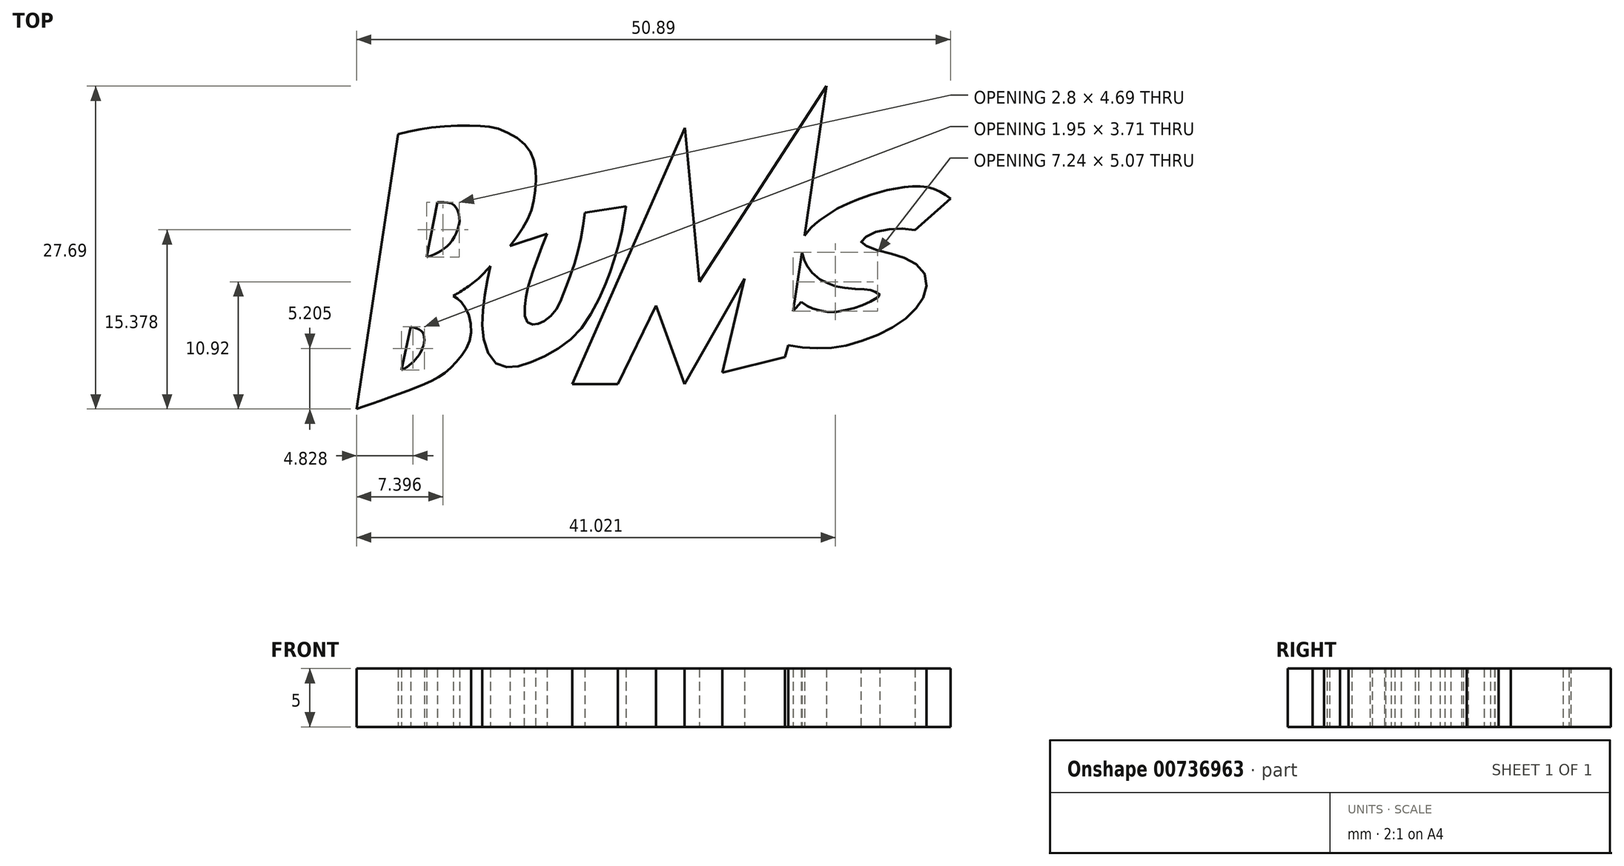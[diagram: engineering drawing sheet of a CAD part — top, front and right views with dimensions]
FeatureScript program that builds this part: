
annotation { "Feature Type Name" : "Feature", "Feature Type Description" : "" }
export const myFeature = defineFeature(function(context is Context, id is Id, definition is map)
    precondition{}
    {
        {
            var Q0;
            Q0=qCreatedBy(makeId("Top.planeOp"),FACE);
            var sketch = newSketch(context, id + "F0", { "sketchPlane" : qUnion([Q0])});
            skLineSegment(sketch, "E0", {"start": v(-15.5, -22.34) * mm, "end": v(-11.93, 1.24) * mm});
            skLineSegment(sketch, "E1", {"start": v(-11.64, -18.99) * mm, "end": v(-10.84, -15.28) * mm});
            skFitSpline(sketch, "E2", {"points": [v(-10.84, -15.28) * mm, v(-10.4, -15.42) * mm, v(-9.9, -15.69) * mm, v(-9.69, -16.35) * mm, v(-9.83, -17.08) * mm, v(-10.2, -17.8) * mm, v(-10.83, -18.47) * mm, v(-11.64, -18.99) * mm], "startDerivative": vector(3.7, -0.9) * mm, "endDerivative": vector(-6.02, -2.49) * mm});
            skLineSegment(sketch, "E3", {"start": v(-9.5, -9.3) * mm, "end": v(-8.56, -4.62) * mm});
            skFitSpline(sketch, "E4", {"points": [v(-8.56, -4.62) * mm, v(-7.96, -4.62) * mm, v(-7.3, -4.75) * mm, v(-6.9, -5.16) * mm, v(-6.7, -5.78) * mm, v(-6.7, -6.45) * mm, v(-6.98, -7.33) * mm, v(-7.5, -8.12) * mm, v(-8.02, -8.6) * mm, v(-8.72, -9.01) * mm, v(-9.5, -9.3) * mm], "startDerivative": vector(6.47, 0.18) * mm, "endDerivative": vector(-7.33, -2.52) * mm});
            skFitSpline(sketch, "E5", {"points": [v(-11.93, 1.24) * mm, v(-8.9, 1.83) * mm, v(-5.24, 1.94) * mm, v(-3.3, 1.67) * mm, v(-1.08, 0.37) * mm, v(-0.22, -1.38) * mm, v(-0.22, -3.86) * mm, v(-0.84, -6.07) * mm, v(-2.35, -8.36) * mm], "startDerivative": vector(20.89, 5.15) * mm, "endDerivative": vector(-13.2, -17.64) * mm});
            skFitSpline(sketch, "E6", {"points": [v(-15.5, -22.34) * mm, v(-13.72, -21.72) * mm, v(-11.31, -20.84) * mm, v(-9.3, -20.04) * mm, v(-7.88, -19.2) * mm, v(-6.62, -17.9) * mm, v(-5.75, -16.26) * mm, v(-5.9, -14.24) * mm, v(-6.62, -13.06) * mm, v(-7.2, -12.64) * mm], "startDerivative": vector(14.72, 5.08) * mm, "endDerivative": vector(-8.03, 4.87) * mm});
            skFitSpline(sketch, "E7", {"points": [v(-4.03, -10.08) * mm, v(-4.45, -12.14) * mm, v(-4.72, -14.5) * mm, v(-4.56, -16.53) * mm, v(-3.76, -18.24) * mm, v(-2.58, -18.74) * mm, v(-1.17, -18.55) * mm, v(0.82, -17.71) * mm, v(2.84, -16.37) * mm, v(4.44, -14.43) * mm, v(5.77, -11.76) * mm, v(6.3, -10.35) * mm, v(6.96, -8.29) * mm, v(7.38, -6.34) * mm, v(7.6, -4.97) * mm], "startDerivative": vector(-6.05, -27.3) * mm, "endDerivative": vector(3.54, 22.1) * mm});
            skFitSpline(sketch, "E8", {"points": [v(0.82, -7.3) * mm, v(-0.33, -10.35) * mm, v(-0.82, -11.99) * mm, v(-1.1, -13.74) * mm, v(-0.86, -14.89) * mm, v(-0.33, -15.08) * mm, v(0.32, -14.93) * mm, v(1.31, -14.2) * mm, v(2.04, -12.94) * mm, v(2.6, -11.45) * mm, v(3.49, -8.82) * mm, v(4.06, -5.5) * mm], "startDerivative": vector(-9.98, -25.95) * mm, "endDerivative": vector(3.45, 26.08) * mm});
            skFitSpline(sketch, "E9", {"points": [v(-4.03, -10.08) * mm, v(-5.06, -11.15) * mm, v(-6.16, -11.99) * mm, v(-7.2, -12.64) * mm], "startDerivative": vector(-2.87, -3.2) * mm, "endDerivative": vector(-3.24, -1.98) * mm});
            skFitSpline(sketch, "E10", {"points": [v(35.4, -4.29) * mm, v(34.16, -3.52) * mm, v(32.44, -3.24) * mm, v(29.92, -3.58) * mm, v(27.79, -4.25) * mm, v(25.97, -5.01) * mm, v(24.62, -5.85) * mm, v(23.48, -6.79) * mm, v(22.89, -7.45) * mm], "startDerivative": vector(-10.2, 7.46) * mm, "endDerivative": vector(-5.81, -7.18) * mm});
            skFitSpline(sketch, "E11", {"points": [v(32.34, -7) * mm, v(31.22, -6.86) * mm, v(30.04, -6.94) * mm, v(28.9, -7.19) * mm, v(28.2, -7.55) * mm, v(27.84, -7.82) * mm, v(27.75, -8.04) * mm, v(28, -8.22) * mm, v(28.3, -8.4) * mm, v(29.3, -8.75) * mm, v(30.76, -9.15) * mm, v(31.83, -9.55) * mm, v(32.88, -10.28) * mm, v(33.32, -11.2) * mm, v(33.28, -12.26) * mm, v(32.86, -13.16) * mm, v(32.1, -14.1) * mm, v(30.78, -15.12) * mm, v(29.24, -15.96) * mm, v(27.35, -16.65) * mm, v(25.69, -17.05) * mm, v(24.37, -17.12) * mm, v(22.85, -17.07) * mm, v(21.51, -16.86) * mm], "startDerivative": vector(-25.16, 4.07) * mm, "endDerivative": vector(-26.73, 5.05) * mm});
            skFitSpline(sketch, "E12", {"points": [v(22.6, -13.16) * mm, v(23.15, -13.52) * mm, v(23.65, -13.73) * mm, v(24.35, -13.92) * mm, v(25.21, -14.03) * mm, v(26.32, -13.86) * mm, v(27.3, -13.63) * mm, v(28.3, -13.23) * mm, v(29.1, -12.8) * mm, v(29.36, -12.55) * mm, v(29.25, -12.47) * mm, v(28.98, -12.29) * mm, v(28.64, -12.14) * mm, v(28.17, -12.08) * mm, v(27.22, -12.05) * mm, v(25.83, -11.87) * mm, v(25.06, -11.62) * mm, v(23.95, -11.04) * mm, v(23.2, -10.2) * mm, v(22.91, -9.7) * mm, v(22.68, -8.88) * mm], "startDerivative": vector(11.84, -8.34) * mm, "endDerivative": vector(-3.82, 16.56) * mm});
            skLineSegment(sketch, "E13", {"start": v(35.4, -4.29) * mm, "end": v(32.34, -7) * mm});
            skLineSegment(sketch, "E14", {"start": v(22.68, -8.88) * mm, "end": v(21.91, -13.96) * mm});
            skLineSegment(sketch, "E15", {"start": v(21.91, -13.96) * mm, "end": v(22.6, -13.16) * mm});
            skLineSegment(sketch, "E16", {"start": v(22.89, -7.45) * mm, "end": v(24.77, 5.35) * mm});
            skLineSegment(sketch, "E17", {"start": v(24.77, 5.35) * mm, "end": v(13.86, -11.42) * mm});
            skLineSegment(sketch, "E18", {"start": v(13.86, -11.42) * mm, "end": v(12.64, 1.76) * mm});
            skLineSegment(sketch, "E19", {"start": v(12.64, 1.76) * mm, "end": v(2.99, -20.21) * mm});
            skLineSegment(sketch, "E20", {"start": v(2.99, -20.21) * mm, "end": v(6.9, -20.21) * mm});
            skLineSegment(sketch, "E21", {"start": v(6.9, -20.21) * mm, "end": v(10.17, -13.48) * mm});
            skLineSegment(sketch, "E22", {"start": v(10.17, -13.48) * mm, "end": v(12.61, -20.21) * mm});
            skLineSegment(sketch, "E23", {"start": v(12.61, -20.21) * mm, "end": v(17.74, -11.13) * mm});
            skLineSegment(sketch, "E24", {"start": v(17.74, -11.13) * mm, "end": v(15.85, -19.22) * mm});
            skLineSegment(sketch, "E25", {"start": v(15.85, -19.22) * mm, "end": v(21.2, -17.87) * mm});
            skLineSegment(sketch, "E26", {"start": v(21.2, -17.87) * mm, "end": v(21.51, -16.86) * mm});
            skLineSegment(sketch, "E27", {"start": v(4.06, -5.5) * mm, "end": v(7.6, -4.97) * mm});
            skLineSegment(sketch, "E28", {"start": v(0.82, -7.3) * mm, "end": v(-2.35, -8.36) * mm});
            skSolve(sketch);
        }
        {
            var Q0;
            Q0=makeQuery(id+"F0.imprint","IMPRINT",FACE,{"disambiguationData":[TD([[makeQuery(id+"F0.imprint","IMPRINT",EDGE,{"derivedFrom":sQuery(id+"F0.wireOp",EDGE,"E0")}),-1.0]])]});
            var Q1;
            Q1=makeQuery(id+"F0.imprint","IMPRINT",FACE,{"disambiguationData":[TD([[makeQuery(id+"F0.imprint","IMPRINT",EDGE,{"derivedFrom":sQuery(id+"F0.wireOp",EDGE,"E10")}),1.0]])]});
            extrude(context, id + "F1", {"entities" : qUnion([Q0, Q1]), "depth" : 5 * mm, "offsetDistance" : 25.4 * mm});
        }
    });
